# Revit family: FP-Revit22-en-RF610ANUB5-ActivesmartRefrigerator-0-90004251A-SG
name_source: partatom
category: Specialty Equipment
units: mm (PartAtom-declared; Revit-internal decimal feet)

## family parameters
Always vertical = Yes
Cut with Voids When Loaded = Yes
Maintain Annotation Orientation = No
OmniClass Number = 23.40.40.11.11.17
OmniClass Title = Refrigerator-Freezer
Part Type = Normal
Room Calculation Point = No
Round Connector Dimension = Use Diameter
Shared = No
Work Plane-Based = No

## types (1)
- RF610ANUB7
    Cavity - Depth = 695 mm  [stored 2.28018 ft]
    Cavity - Height = 1815 mm  [stored 5.95472 ft]
    Cavity - Width = 940 mm  [stored 3.08399 ft]
    Chassis - Depth = 625 mm  [stored 2.05052 ft]
    Chassis - Height = 1737 mm  [stored 5.69882 ft]
    Chassis - Width = 900 mm  [stored 2.95276 ft]
    Connector Description - Electrical = 230 V, 50 Hz
    Connector Description - Water = Ø6mm (1/4”) quick connect, Max Supply Pressure 120psi (827kPa)
    Default Elevation = 0 mm  [stored 0 ft]
    Description = 90cm French Door Refrigerator Freezer, Ice and Water
    Manufacturer = Fisher & Paykel Appliances
    Material - Body = Fisher & Paykel - Grey
    Material - Door Front = Fisher & Paykel - Stainless Steel, Dark
    Material - Door Structure = Fisher & Paykel - White
    Material - Trim = Fisher & Paykel - Aluminium, Dark
    Model = RF610ANUB7
    Product - Depth = 695 mm  [stored 2.28018 ft]
    Product - Height = 1795 mm
    Product - Width = 900 mm  [stored 2.95276 ft]
    URL = www.fisherpaykel.com
    Visibility - Clearance Required = Yes

note: [stored X ft] marks values corroborated as IEEE doubles in the binary element streams (Revit-internal decimal feet)

## geometry (parser evidence)
native form markers: Sweep x6
no freeform markers — native parametric forms only
